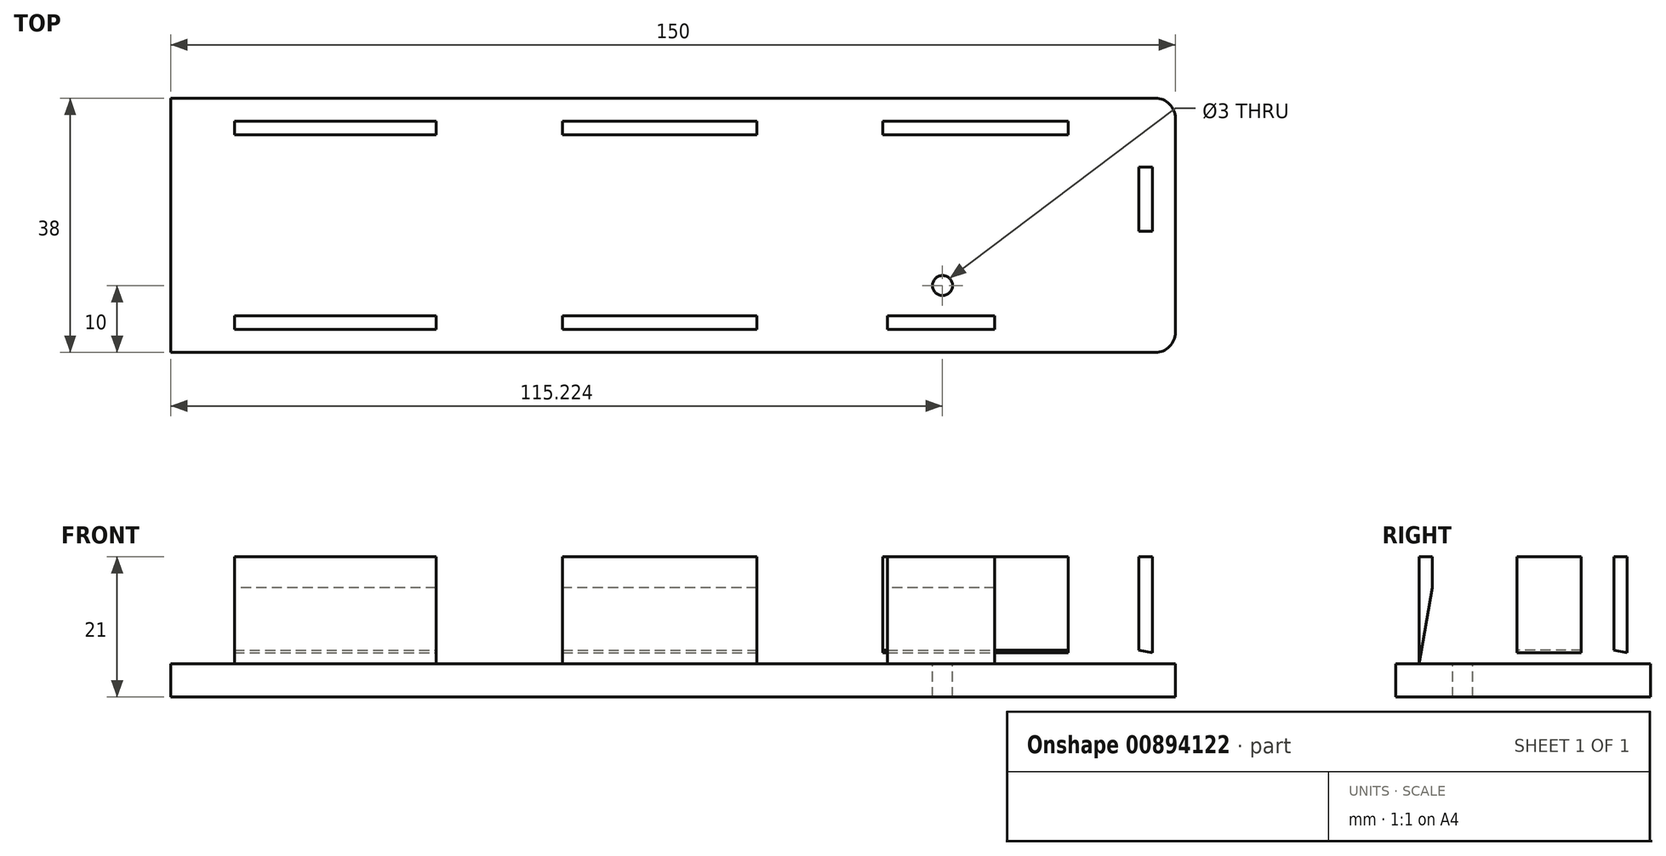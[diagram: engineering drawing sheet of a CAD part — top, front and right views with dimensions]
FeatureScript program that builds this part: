
annotation { "Feature Type Name" : "Feature", "Feature Type Description" : "" }
export const myFeature = defineFeature(function(context is Context, id is Id, definition is map)
    precondition{}
    {
        {
            var Q0;
            Q0=qCreatedBy(makeId("Top.planeOp"),FACE);
            var sketch = newSketch(context, id + "F0", { "sketchPlane" : qUnion([Q0])});
            skLineSegment(sketch, "E0.bottom", {"start": v(150, 19) * mm, "end": v(0, 19) * mm});
            skLineSegment(sketch, "E0.top", {"start": v(150, -19) * mm, "end": v(0, -19) * mm});
            skLineSegment(sketch, "E0.left", {"start": v(150, 19) * mm, "end": v(150, -19) * mm});
            skLineSegment(sketch, "E0.right", {"start": v(0, 19) * mm, "end": v(0, -19) * mm});
            skPoint(sketch, "E0.middle", {"position": v(75, 0) * mm});
            skSolve(sketch);
        }
        {
            var Q0;
            Q0=makeQuery(id+"F0.imprint","IMPRINT",FACE,{"disambiguationData":[TD([[makeQuery(id+"F0.imprint","IMPRINT",EDGE,{"derivedFrom":sQuery(id+"F0.wireOp",EDGE,"E0.bottom")}),1.0]])]});
            extrude(context, id + "F1", {"entities" : qUnion([Q0]), "depth" : 5 * mm, "offsetDistance" : 25 * mm});
        }
        {
            var Q0;
            Q0=makeQuery(id+"F1.opExtrude","SWEPT_EDGE",EDGE,{"disambiguationData":[OSD([sQuery(id+"F0.wireOp",EDGE,"E0.top"),sQuery(id+"F0.wireOp",EDGE,"E0.left")])]});
            var Q1;
            Q1=makeQuery(id+"F1.opExtrude","SWEPT_EDGE",EDGE,{"disambiguationData":[OSD([sQuery(id+"F0.wireOp",EDGE,"E0.bottom"),sQuery(id+"F0.wireOp",EDGE,"E0.left")])]});
            fillet(context, id + "F2", {"entities" : qUnion([Q0, Q1]), "radius" : 3 * mm, "tangentPropagation" : true, "allowEdgeOverflow" : false});
        }
        {
            assignVariable(context, id + "F3", {"name" : "tabh", "anyValue" : 16});
        }
        {
            var Q0;
            Q0=makeQuery(id+"F1.opExtrude","CAP_FACE",FACE,{"disambiguationData":[OSD([sQuery(id+"F0.wireOp",EDGE,"E0.bottom"),sQuery(id+"F0.wireOp",EDGE,"E0.top"),sQuery(id+"F0.wireOp",EDGE,"E0.left"),sQuery(id+"F0.wireOp",EDGE,"E0.right")])],"isStart":false});
            var sketch = newSketch(context, id + "F4", { "sketchPlane" : qUnion([Q0])});
            skLineSegment(sketch, "E1.bottom", {"start": v(106.3, 15.55) * mm, "end": v(134, 15.55) * mm});
            skLineSegment(sketch, "E1.top", {"start": v(106.3, 13.55) * mm, "end": v(134, 13.55) * mm});
            skLineSegment(sketch, "E1.left", {"start": v(106.3, 15.55) * mm, "end": v(106.3, 13.55) * mm});
            skLineSegment(sketch, "E1.right", {"start": v(134, 15.55) * mm, "end": v(134, 13.55) * mm});
            skSolve(sketch);
        }
        {
            var Q0;
            Q0=makeQuery(id+"F4.imprint","IMPRINT",FACE,{"disambiguationData":[TD([[makeQuery(id+"F4.imprint","IMPRINT",EDGE,{"derivedFrom":sQuery(id+"F4.wireOp",EDGE,"E1.bottom")}),-1.0]])]});
            extrude(context, id + "F5", {"entities" : qUnion([Q0]), "depth" : (getVariable(context, 'tabh')) * mm, "offsetDistance" : 25 * mm});
        }
        {
            var Q0;
            Q0=makeQuery(id+"F1.opExtrude","CAP_FACE",FACE,{"disambiguationData":[OSD([sQuery(id+"F0.wireOp",EDGE,"E0.bottom"),sQuery(id+"F0.wireOp",EDGE,"E0.top"),sQuery(id+"F0.wireOp",EDGE,"E0.left"),sQuery(id+"F0.wireOp",EDGE,"E0.right")])],"isStart":false});
            var sketch = newSketch(context, id + "F6", { "sketchPlane" : qUnion([Q0])});
            skLineSegment(sketch, "E2.bottom", {"start": v(58.5, 15.55) * mm, "end": v(87.5, 15.55) * mm});
            skLineSegment(sketch, "E2.top", {"start": v(58.5, 13.55) * mm, "end": v(87.5, 13.55) * mm});
            skLineSegment(sketch, "E2.left", {"start": v(58.5, 15.55) * mm, "end": v(58.5, 13.55) * mm});
            skLineSegment(sketch, "E2.right", {"start": v(87.5, 15.55) * mm, "end": v(87.5, 13.55) * mm});
            skSolve(sketch);
        }
        {
            var Q0;
            Q0=makeQuery(id+"F6.imprint","IMPRINT",FACE,{"disambiguationData":[TD([[makeQuery(id+"F6.imprint","IMPRINT",EDGE,{"derivedFrom":sQuery(id+"F6.wireOp",EDGE,"E2.bottom")}),-1.0]])]});
            extrude(context, id + "F7", {"entities" : qUnion([Q0]), "depth" : (getVariable(context, 'tabh')) * mm, "offsetDistance" : 25 * mm});
        }
        {
            var Q0;
            Q0=makeQuery(id+"F1.opExtrude","CAP_FACE",FACE,{"disambiguationData":[OSD([sQuery(id+"F0.wireOp",EDGE,"E0.bottom"),sQuery(id+"F0.wireOp",EDGE,"E0.top"),sQuery(id+"F0.wireOp",EDGE,"E0.left"),sQuery(id+"F0.wireOp",EDGE,"E0.right")])],"isStart":false});
            var sketch = newSketch(context, id + "F8", { "sketchPlane" : qUnion([Q0])});
            skLineSegment(sketch, "E3.bottom", {"start": v(9.5, 15.55) * mm, "end": v(39.6, 15.55) * mm});
            skLineSegment(sketch, "E3.top", {"start": v(9.5, 13.55) * mm, "end": v(39.6, 13.55) * mm});
            skLineSegment(sketch, "E3.left", {"start": v(9.5, 15.55) * mm, "end": v(9.5, 13.55) * mm});
            skLineSegment(sketch, "E3.right", {"start": v(39.6, 15.55) * mm, "end": v(39.6, 13.55) * mm});
            skSolve(sketch);
        }
        {
            var Q0;
            Q0=makeQuery(id+"F8.imprint","IMPRINT",FACE,{"disambiguationData":[TD([[makeQuery(id+"F8.imprint","IMPRINT",EDGE,{"derivedFrom":sQuery(id+"F8.wireOp",EDGE,"E3.bottom")}),-1.0]])]});
            extrude(context, id + "F9", {"entities" : qUnion([Q0]), "depth" : (getVariable(context, 'tabh')) * mm, "offsetDistance" : 25 * mm});
        }
        {
            var Q0;
            Q0=makeQuery(id+"F9.opExtrude","SWEPT_BODY",BODY,{"disambiguationData":[OSD([sQuery(id+"F8.wireOp",EDGE,"E3.bottom"),sQuery(id+"F8.wireOp",EDGE,"E3.top"),sQuery(id+"F8.wireOp",EDGE,"E3.left"),sQuery(id+"F8.wireOp",EDGE,"E3.right")])]});
            var Q1;
            Q1=makeQuery(id+"F7.opExtrude","SWEPT_BODY",BODY,{"disambiguationData":[OSD([sQuery(id+"F6.wireOp",EDGE,"E2.bottom"),sQuery(id+"F6.wireOp",EDGE,"E2.top"),sQuery(id+"F6.wireOp",EDGE,"E2.left"),sQuery(id+"F6.wireOp",EDGE,"E2.right")])]});
            var Q2;
            Q2=qCreatedBy(makeId("Front.planeOp"),FACE);
            mirror(context, id + "F10", {"entities" : qUnion([Q0, Q1]), "mirrorPlane" : qUnion([Q2])});
        }
        {
            var Q0;
            Q0=makeQuery(id+"F1.opExtrude","CAP_FACE",FACE,{"disambiguationData":[OSD([sQuery(id+"F0.wireOp",EDGE,"E0.bottom"),sQuery(id+"F0.wireOp",EDGE,"E0.top"),sQuery(id+"F0.wireOp",EDGE,"E0.left"),sQuery(id+"F0.wireOp",EDGE,"E0.right")])],"isStart":false});
            var sketch = newSketch(context, id + "F11", { "sketchPlane" : qUnion([Q0])});
            skLineSegment(sketch, "E4.bottom", {"start": v(107, -13.55) * mm, "end": v(123, -13.55) * mm});
            skLineSegment(sketch, "E4.top", {"start": v(107, -15.55) * mm, "end": v(123, -15.55) * mm});
            skLineSegment(sketch, "E4.left", {"start": v(107, -13.55) * mm, "end": v(107, -15.55) * mm});
            skLineSegment(sketch, "E4.right", {"start": v(123, -13.55) * mm, "end": v(123, -15.55) * mm});
            skSolve(sketch);
        }
        {
            var Q0;
            Q0=makeQuery(id+"F11.imprint","IMPRINT",FACE,{"disambiguationData":[TD([[makeQuery(id+"F11.imprint","IMPRINT",EDGE,{"derivedFrom":sQuery(id+"F11.wireOp",EDGE,"E4.bottom")}),-1.0]])]});
            extrude(context, id + "F12", {"entities" : qUnion([Q0]), "depth" : (getVariable(context, 'tabh')) * mm, "offsetDistance" : 25 * mm});
        }
        {
            var Q0;
            Q0=makeQuery(id+"F1.opExtrude","CAP_FACE",FACE,{"disambiguationData":[OSD([sQuery(id+"F0.wireOp",EDGE,"E0.bottom"),sQuery(id+"F0.wireOp",EDGE,"E0.top"),sQuery(id+"F0.wireOp",EDGE,"E0.left"),sQuery(id+"F0.wireOp",EDGE,"E0.right")])],"isStart":false});
            var sketch = newSketch(context, id + "F13", { "sketchPlane" : qUnion([Q0])});
            skLineSegment(sketch, "E5.bottom", {"start": v(144.55, 8.7) * mm, "end": v(146.55, 8.7) * mm});
            skLineSegment(sketch, "E5.top", {"start": v(144.55, -0.9) * mm, "end": v(146.55, -0.9) * mm});
            skLineSegment(sketch, "E5.left", {"start": v(144.55, 8.7) * mm, "end": v(144.55, -0.9) * mm});
            skLineSegment(sketch, "E5.right", {"start": v(146.55, 8.7) * mm, "end": v(146.55, -0.9) * mm});
            skSolve(sketch);
        }
        {
            var Q0;
            Q0=makeQuery(id+"F13.imprint","IMPRINT",FACE,{"disambiguationData":[TD([[makeQuery(id+"F13.imprint","IMPRINT",EDGE,{"derivedFrom":sQuery(id+"F13.wireOp",EDGE,"E5.bottom")}),-1.0]])]});
            extrude(context, id + "F14", {"entities" : qUnion([Q0]), "depth" : (getVariable(context, 'tabh')) * mm, "offsetDistance" : 25 * mm});
        }
        {
            var Q0;
            Q0=makeQuery(id+"F1.opExtrude","CAP_FACE",FACE,{"disambiguationData":[OSD([sQuery(id+"F0.wireOp",EDGE,"E0.bottom"),sQuery(id+"F0.wireOp",EDGE,"E0.top"),sQuery(id+"F0.wireOp",EDGE,"E0.left"),sQuery(id+"F0.wireOp",EDGE,"E0.right")])],"isStart":false});
            var sketch = newSketch(context, id + "F15", { "sketchPlane" : qUnion([Q0])});
            skCircle(sketch, "E6", {"center": v(115.22, -9) * mm, "radius": 1.5 * mm});
            skSolve(sketch);
        }
        {
            var Q0;
            Q0=makeQuery(id+"F15.imprint","IMPRINT",FACE,{"disambiguationData":[TD([[makeQuery(id+"F15.imprint","IMPRINT",EDGE,{"derivedFrom":sQuery(id+"F15.wireOp",EDGE,"E6")}),1.0]])]});
            extrude(context, id + "F16", {"entities" : qUnion([Q0]), "operationType" : NewBodyOperationType.REMOVE, "oppositeDirection" : true, "depth" : 25 * mm, "offsetDistance" : 25 * mm});
        }
        {
            var Q0;
            Q0=makeQuery(id+"F12.opExtrude","CAP_EDGE",EDGE,{"disambiguationData":[OSD([sQuery(id+"F11.wireOp",EDGE,"E4.bottom")])],"isStart":true});
            var Q1;
            Q1=makeQuery(id+"F10.opPattern","COPY",EDGE,{"derivedFrom":makeQuery(id+"F7.opExtrude","CAP_EDGE",EDGE,{"disambiguationData":[OSD([sQuery(id+"F6.wireOp",EDGE,"E2.top")])],"isStart":true}),"instanceName":"1"});
            var Q2;
            Q2=makeQuery(id+"F10.opPattern","COPY",EDGE,{"derivedFrom":makeQuery(id+"F9.opExtrude","CAP_EDGE",EDGE,{"disambiguationData":[OSD([sQuery(id+"F8.wireOp",EDGE,"E3.top")])],"isStart":true}),"instanceName":"1"});
            var Q3;
            Q3=makeQuery(id+"F9.opExtrude","CAP_EDGE",EDGE,{"disambiguationData":[OSD([sQuery(id+"F8.wireOp",EDGE,"E3.top")])],"isStart":true});
            var Q4;
            Q4=makeQuery(id+"F7.opExtrude","CAP_EDGE",EDGE,{"disambiguationData":[OSD([sQuery(id+"F6.wireOp",EDGE,"E2.top")])],"isStart":true});
            var Q5;
            Q5=makeQuery(id+"F5.opExtrude","CAP_EDGE",EDGE,{"disambiguationData":[OSD([sQuery(id+"F4.wireOp",EDGE,"E1.top")])],"isStart":true});
            var Q6;
            Q6=makeQuery(id+"F14.opExtrude","CAP_EDGE",EDGE,{"disambiguationData":[OSD([sQuery(id+"F13.wireOp",EDGE,"E5.left")])],"isStart":true});
            chamfer(context, id + "F17", {"entities" : qUnion([Q0, Q1, Q2, Q3, Q4, Q5, Q6]), "chamferType" : ChamferType.OFFSET_ANGLE, "width" : 2 * mm, "oppositeDirection" : false, "angle" : 80 * degree, "tangentPropagation" : true});
        }
    });
